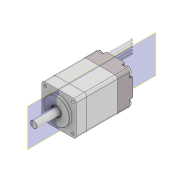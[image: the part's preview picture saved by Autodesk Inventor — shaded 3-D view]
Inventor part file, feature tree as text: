
AUTODESK INVENTOR PART (.ipt)
format: ipt  version: 2022 (Build 260153000, 153)  size: 350,720 bytes
history: native  units: mm
features: other x13, plane x1
ambient origin geometry x8: Origin, YZ Plane, XZ Plane, XY Plane, X Axis, Y Axis, Z Axis, Center Point
bodies: Solid1 (feature_tree), Solid2 (feature_tree), Solid3 (feature_tree), Solid4 (feature_tree), Solid5 (feature_tree), Solid6 (feature_tree), Solid7 (feature_tree), Solid8 (feature_tree), Solid9 (feature_tree), Solid10 (feature_tree), Solid11 (feature_tree), Solid12 (feature_tree), Solid13 (feature_tree)
feature tree (14):
  plane  "Work Plane1"
  other  "Stator_ST2018_S_1:1"
  other  "Frontcap_ST2018_1:1"
  other  "shaft_forward_ST2018_1:1"
  other  "leads_4_ST2018_1:1"
  other  "leads_4_ST2018_1:2"
  other  "leads_4_ST2018_1:3"
  other  "leads_4_ST2018_1:4"
  other  "leads_4_ST2018_1:5"
  other  "Schraubenkopf_1:1"
  other  "Schraubenkopf_2:1"
  other  "Schraubenkopf_3:1"
  other  "Schraubenkopf_4:1"
  other  "Endkappe_ST2018_A_1:1"
